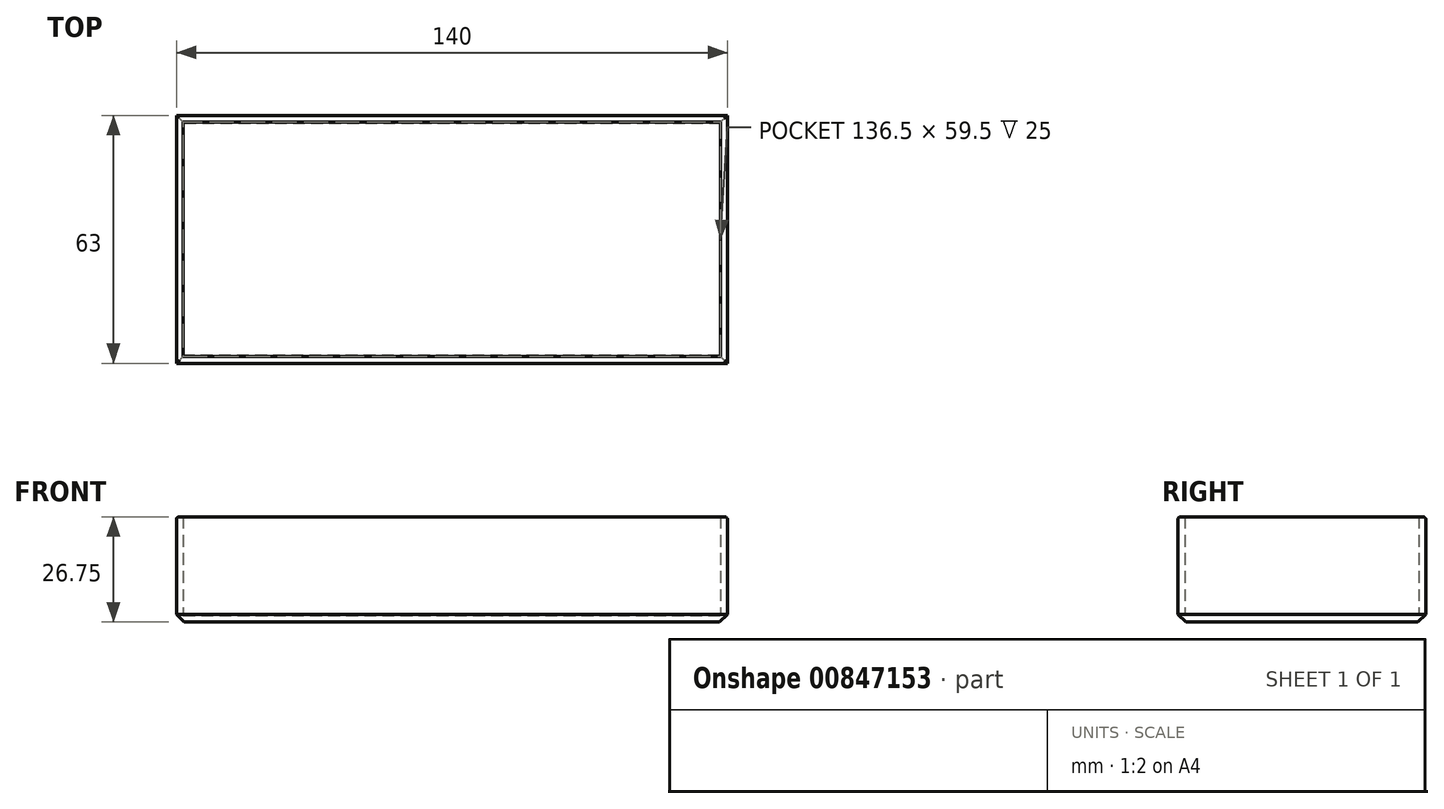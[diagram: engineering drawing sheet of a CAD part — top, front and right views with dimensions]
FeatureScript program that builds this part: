
annotation { "Feature Type Name" : "Feature", "Feature Type Description" : "" }
export const myFeature = defineFeature(function(context is Context, id is Id, definition is map)
    precondition{}
    {
        {
            var Q0;
            Q0=qCreatedBy(makeId("Top.planeOp"),FACE);
            var sketch = newSketch(context, id + "F0", { "sketchPlane" : qUnion([Q0])});
            skLineSegment(sketch, "E0.bottom", {"start": v(-67.25, -1.44) * mm, "end": v(72.75, -1.44) * mm});
            skLineSegment(sketch, "E0.top", {"start": v(-67.25, -64.44) * mm, "end": v(72.75, -64.44) * mm});
            skLineSegment(sketch, "E0.left", {"start": v(-67.25, -1.44) * mm, "end": v(-67.25, -64.44) * mm});
            skLineSegment(sketch, "E0.right", {"start": v(72.75, -1.44) * mm, "end": v(72.75, -64.44) * mm});
            skSolve(sketch);
        }
        {
            var Q0;
            Q0=makeQuery(id+"F0.imprint","IMPRINT",FACE,{"disambiguationData":[TD([[makeQuery(id+"F0.imprint","IMPRINT",EDGE,{"derivedFrom":sQuery(id+"F0.wireOp",EDGE,"E0.bottom")}),-1.0]])]});
            extrude(context, id + "F1", {"entities" : qUnion([Q0]), "depth" : 1.75 * mm, "offsetDistance" : 25 * mm});
        }
        {
            var Q0;
            Q0=makeQuery(id+"F1.opExtrude","CAP_FACE",FACE,{"disambiguationData":[OSD([sQuery(id+"F0.wireOp",EDGE,"E0.bottom"),sQuery(id+"F0.wireOp",EDGE,"E0.top"),sQuery(id+"F0.wireOp",EDGE,"E0.left"),sQuery(id+"F0.wireOp",EDGE,"E0.right")])],"isStart":false});
            var sketch = newSketch(context, id + "F2", { "sketchPlane" : qUnion([Q0])});
            skLineSegment(sketch, "E1.bottom", {"start": v(-67.25, -1.44) * mm, "end": v(72.75, -1.44) * mm});
            skLineSegment(sketch, "E1.top", {"start": v(-67.25, -64.44) * mm, "end": v(72.75, -64.44) * mm});
            skLineSegment(sketch, "E1.left", {"start": v(-67.25, -1.44) * mm, "end": v(-67.25, -64.44) * mm});
            skLineSegment(sketch, "E1.right", {"start": v(72.75, -1.44) * mm, "end": v(72.75, -64.44) * mm});
            skLineSegment(sketch, "E2.bottom", {"start": v(-65.5, -3.2) * mm, "end": v(71, -3.2) * mm});
            skLineSegment(sketch, "E2.top", {"start": v(-65.5, -62.7) * mm, "end": v(71, -62.7) * mm});
            skLineSegment(sketch, "E2.left", {"start": v(-65.5, -3.2) * mm, "end": v(-65.5, -62.7) * mm});
            skLineSegment(sketch, "E2.right", {"start": v(71, -3.2) * mm, "end": v(71, -62.7) * mm});
            skSolve(sketch);
        }
        {
            var Q0;
            Q0=makeQuery(id+"F2.imprint","IMPRINT",FACE,{"disambiguationData":[TD([[makeQuery(id+"F2.imprint","IMPRINT",EDGE,{"derivedFrom":sQuery(id+"F2.wireOp",EDGE,"E1.bottom")}),-1.0]])]});
            extrude(context, id + "F3", {"entities" : qUnion([Q0]), "operationType" : NewBodyOperationType.ADD, "depth" : 25 * mm, "offsetDistance" : 25 * mm});
        }
        {
            var Q0;
            Q0=makeQuery(id+"F3.opExtrude","CAP_EDGE",EDGE,{"disambiguationData":[OSD([sQuery(id+"F2.wireOp",EDGE,"E1.bottom")])],"isStart":false});
            var Q1;
            Q1=makeQuery(id+"F3.opExtrude","CAP_EDGE",EDGE,{"disambiguationData":[OSD([sQuery(id+"F2.wireOp",EDGE,"E1.right")])],"isStart":false});
            var Q2;
            Q2=makeQuery(id+"F3.opExtrude","CAP_EDGE",EDGE,{"disambiguationData":[OSD([sQuery(id+"F2.wireOp",EDGE,"E1.top")])],"isStart":false});
            var Q3;
            Q3=makeQuery(id+"F3.opExtrude","CAP_EDGE",EDGE,{"disambiguationData":[OSD([sQuery(id+"F2.wireOp",EDGE,"E1.left")])],"isStart":false});
            var Q4;
            {var subQ0=sQuery(id+"F2.wireOp",EDGE,"E1.left");var subQ1=sQuery(id+"F2.wireOp",EDGE,"E1.bottom");Q4=makeQuery(id+"F62N5uDxJauJSGm_1.opFillet","BLEND_EDGE",EDGE,{"blendedFrom":[makeQuery(id+"F3.boolean.opBoolean","MERGE",EDGE,{"derivedFrom":[makeQuery(id+"F1.opExtrude","SWEPT_EDGE",EDGE,{"disambiguationData":[OSD([sQuery(id+"F0.wireOp",EDGE,"E0.bottom"),sQuery(id+"F0.wireOp",EDGE,"E0.left")])]}),makeQuery(id+"F3.opExtrude","SWEPT_EDGE",EDGE,{"disambiguationData":[OSD([subQ1,subQ0])]})]}),makeQuery(id+"F3.opExtrude","CAP_FACE",FACE,{"disambiguationData":[OSD([subQ1,sQuery(id+"F2.wireOp",EDGE,"E1.top"),subQ0,sQuery(id+"F2.wireOp",EDGE,"E1.right"),sQuery(id+"F2.wireOp",EDGE,"E2.bottom"),sQuery(id+"F2.wireOp",EDGE,"E2.top"),sQuery(id+"F2.wireOp",EDGE,"E2.left"),sQuery(id+"F2.wireOp",EDGE,"E2.right")])],"isStart":false})],"blendedInto":[makeQuery(id+"F3.opExtrude","CAP_FACE",FACE,{"disambiguationData":[OSD([subQ1,sQuery(id+"F2.wireOp",EDGE,"E1.top"),subQ0,sQuery(id+"F2.wireOp",EDGE,"E1.right"),sQuery(id+"F2.wireOp",EDGE,"E2.bottom"),sQuery(id+"F2.wireOp",EDGE,"E2.top"),sQuery(id+"F2.wireOp",EDGE,"E2.left"),sQuery(id+"F2.wireOp",EDGE,"E2.right")])],"isStart":false})]});}
            var Q5;
            {var subQ0=sQuery(id+"F2.wireOp",EDGE,"E1.right");var subQ1=sQuery(id+"F2.wireOp",EDGE,"E1.bottom");Q5=makeQuery(id+"F62N5uDxJauJSGm_1.opFillet","BLEND_EDGE",EDGE,{"blendedFrom":[makeQuery(id+"F3.boolean.opBoolean","MERGE",EDGE,{"derivedFrom":[makeQuery(id+"F1.opExtrude","SWEPT_EDGE",EDGE,{"disambiguationData":[OSD([sQuery(id+"F0.wireOp",EDGE,"E0.bottom"),sQuery(id+"F0.wireOp",EDGE,"E0.right")])]}),makeQuery(id+"F3.opExtrude","SWEPT_EDGE",EDGE,{"disambiguationData":[OSD([subQ1,subQ0])]})]}),makeQuery(id+"F3.opExtrude","CAP_FACE",FACE,{"disambiguationData":[OSD([subQ1,sQuery(id+"F2.wireOp",EDGE,"E1.top"),sQuery(id+"F2.wireOp",EDGE,"E1.left"),subQ0,sQuery(id+"F2.wireOp",EDGE,"E2.bottom"),sQuery(id+"F2.wireOp",EDGE,"E2.top"),sQuery(id+"F2.wireOp",EDGE,"E2.left"),sQuery(id+"F2.wireOp",EDGE,"E2.right")])],"isStart":false})],"blendedInto":[makeQuery(id+"F3.opExtrude","CAP_FACE",FACE,{"disambiguationData":[OSD([subQ1,sQuery(id+"F2.wireOp",EDGE,"E1.top"),sQuery(id+"F2.wireOp",EDGE,"E1.left"),subQ0,sQuery(id+"F2.wireOp",EDGE,"E2.bottom"),sQuery(id+"F2.wireOp",EDGE,"E2.top"),sQuery(id+"F2.wireOp",EDGE,"E2.left"),sQuery(id+"F2.wireOp",EDGE,"E2.right")])],"isStart":false})]});}
            var Q6;
            {var subQ0=sQuery(id+"F2.wireOp",EDGE,"E1.right");var subQ1=sQuery(id+"F2.wireOp",EDGE,"E1.top");Q6=makeQuery(id+"F62N5uDxJauJSGm_1.opFillet","BLEND_EDGE",EDGE,{"blendedFrom":[makeQuery(id+"F3.boolean.opBoolean","MERGE",EDGE,{"derivedFrom":[makeQuery(id+"F1.opExtrude","SWEPT_EDGE",EDGE,{"disambiguationData":[OSD([sQuery(id+"F0.wireOp",EDGE,"E0.top"),sQuery(id+"F0.wireOp",EDGE,"E0.right")])]}),makeQuery(id+"F3.opExtrude","SWEPT_EDGE",EDGE,{"disambiguationData":[OSD([subQ1,subQ0])]})]}),makeQuery(id+"F3.opExtrude","CAP_FACE",FACE,{"disambiguationData":[OSD([sQuery(id+"F2.wireOp",EDGE,"E1.bottom"),subQ1,sQuery(id+"F2.wireOp",EDGE,"E1.left"),subQ0,sQuery(id+"F2.wireOp",EDGE,"E2.bottom"),sQuery(id+"F2.wireOp",EDGE,"E2.top"),sQuery(id+"F2.wireOp",EDGE,"E2.left"),sQuery(id+"F2.wireOp",EDGE,"E2.right")])],"isStart":false})],"blendedInto":[makeQuery(id+"F3.opExtrude","CAP_FACE",FACE,{"disambiguationData":[OSD([sQuery(id+"F2.wireOp",EDGE,"E1.bottom"),subQ1,sQuery(id+"F2.wireOp",EDGE,"E1.left"),subQ0,sQuery(id+"F2.wireOp",EDGE,"E2.bottom"),sQuery(id+"F2.wireOp",EDGE,"E2.top"),sQuery(id+"F2.wireOp",EDGE,"E2.left"),sQuery(id+"F2.wireOp",EDGE,"E2.right")])],"isStart":false})]});}
            var Q7;
            {var subQ0=sQuery(id+"F2.wireOp",EDGE,"E1.left");var subQ1=sQuery(id+"F2.wireOp",EDGE,"E1.top");Q7=makeQuery(id+"F62N5uDxJauJSGm_1.opFillet","BLEND_EDGE",EDGE,{"blendedFrom":[makeQuery(id+"F3.boolean.opBoolean","MERGE",EDGE,{"derivedFrom":[makeQuery(id+"F1.opExtrude","SWEPT_EDGE",EDGE,{"disambiguationData":[OSD([sQuery(id+"F0.wireOp",EDGE,"E0.top"),sQuery(id+"F0.wireOp",EDGE,"E0.left")])]}),makeQuery(id+"F3.opExtrude","SWEPT_EDGE",EDGE,{"disambiguationData":[OSD([subQ1,subQ0])]})]}),makeQuery(id+"F3.opExtrude","CAP_FACE",FACE,{"disambiguationData":[OSD([sQuery(id+"F2.wireOp",EDGE,"E1.bottom"),subQ1,subQ0,sQuery(id+"F2.wireOp",EDGE,"E1.right"),sQuery(id+"F2.wireOp",EDGE,"E2.bottom"),sQuery(id+"F2.wireOp",EDGE,"E2.top"),sQuery(id+"F2.wireOp",EDGE,"E2.left"),sQuery(id+"F2.wireOp",EDGE,"E2.right")])],"isStart":false})],"blendedInto":[makeQuery(id+"F3.opExtrude","CAP_FACE",FACE,{"disambiguationData":[OSD([sQuery(id+"F2.wireOp",EDGE,"E1.bottom"),subQ1,subQ0,sQuery(id+"F2.wireOp",EDGE,"E1.right"),sQuery(id+"F2.wireOp",EDGE,"E2.bottom"),sQuery(id+"F2.wireOp",EDGE,"E2.top"),sQuery(id+"F2.wireOp",EDGE,"E2.left"),sQuery(id+"F2.wireOp",EDGE,"E2.right")])],"isStart":false})]});}
            fillet(context, id + "F4", {"entities" : qUnion([Q0, Q1, Q2, Q3, Q4, Q5, Q6, Q7]), "radius" : .7 * mm, "tangentPropagation" : true, "allowEdgeOverflow" : false});
        }
        {
            var Q0;
            Q0=makeQuery(id+"F1.opExtrude","CAP_FACE",FACE,{"disambiguationData":[OSD([sQuery(id+"F0.wireOp",EDGE,"E0.bottom"),sQuery(id+"F0.wireOp",EDGE,"E0.top"),sQuery(id+"F0.wireOp",EDGE,"E0.left"),sQuery(id+"F0.wireOp",EDGE,"E0.right")])],"isStart":true});
            chamfer(context, id + "F5", {"entities" : qUnion([Q0]), "width" : 2 * mm, "tangentPropagation" : true});
        }
    });
